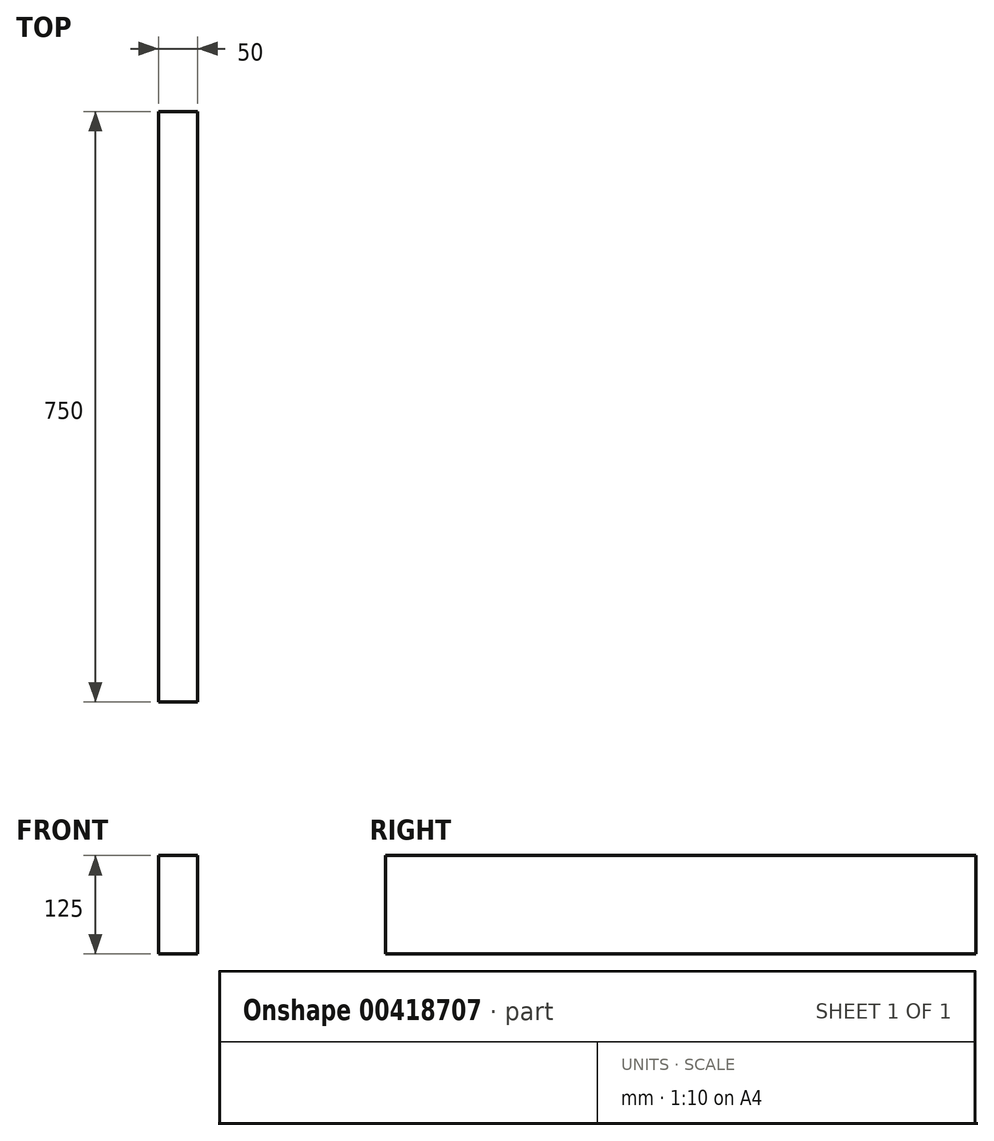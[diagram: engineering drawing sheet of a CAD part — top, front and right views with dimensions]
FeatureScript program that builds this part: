
annotation { "Feature Type Name" : "Feature", "Feature Type Description" : "" }
export const myFeature = defineFeature(function(context is Context, id is Id, definition is map)
    precondition{}
    {
        {
            var Q0;
            Q0=qCreatedBy(makeId("Front.planeOp"),FACE);
            var sketch = newSketch(context, id + "F0", { "sketchPlane" : qUnion([Q0])});
            skLineSegment(sketch, "E0.bottom", {"start": v(25, 62.5) * mm, "end": v(-25, 62.5) * mm});
            skLineSegment(sketch, "E0.top", {"start": v(25, -62.5) * mm, "end": v(-25, -62.5) * mm});
            skLineSegment(sketch, "E0.left", {"start": v(25, 62.5) * mm, "end": v(25, -62.5) * mm});
            skLineSegment(sketch, "E0.right", {"start": v(-25, 62.5) * mm, "end": v(-25, -62.5) * mm});
            skPoint(sketch, "E0.middle", {"position": v(0, 0) * mm});
            skSolve(sketch);
        }
        {
            var Q0;
            Q0 = qSketchRegion(id + "F0", true);
            extrude(context, id + "F1", {"entities" : qUnion([Q0]), "depth" : 750 * mm});
        }
    });
